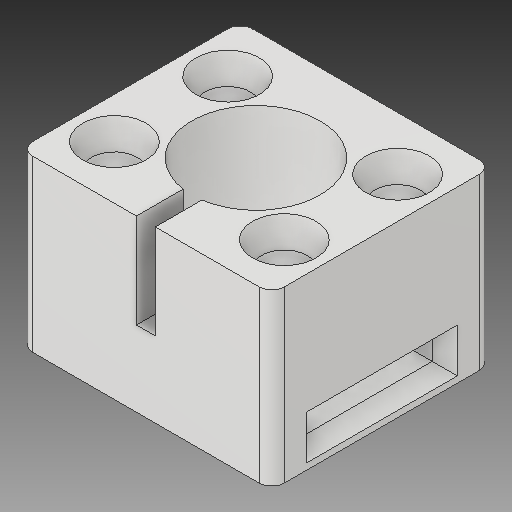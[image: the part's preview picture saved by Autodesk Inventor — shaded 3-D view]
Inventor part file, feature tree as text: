
AUTODESK INVENTOR PART (.ipt)
format: ipt  version: 2019 (Build 230136000, 136)  size: 206,336 bytes
history: native  units: mm
features: sketch x9, other x3, plane x1
ambient origin geometry x8: Origin, YZ Plane, XZ Plane, XY Plane, X Axis, Y Axis, Z Axis, Center Point
bodies: Solid1 (feature_tree)
feature tree (13):
  other  "Electromagnet Block.ipt"
  other  "Solid1::Electromagnet Block.ipt"
  other  "TaggingFeature1"
  sketch  "Sketch1"  dims[d0=10.0mm]
  sketch  "Sketch2"
  sketch  "Sketch3"
  sketch  "Sketch5"
  sketch  "Sketch6"
  sketch  "Sketch7"
  sketch  "Sketch8"
  sketch  "Sketch9"
  sketch  "Sketch10"
  plane  "Work Plane1"
